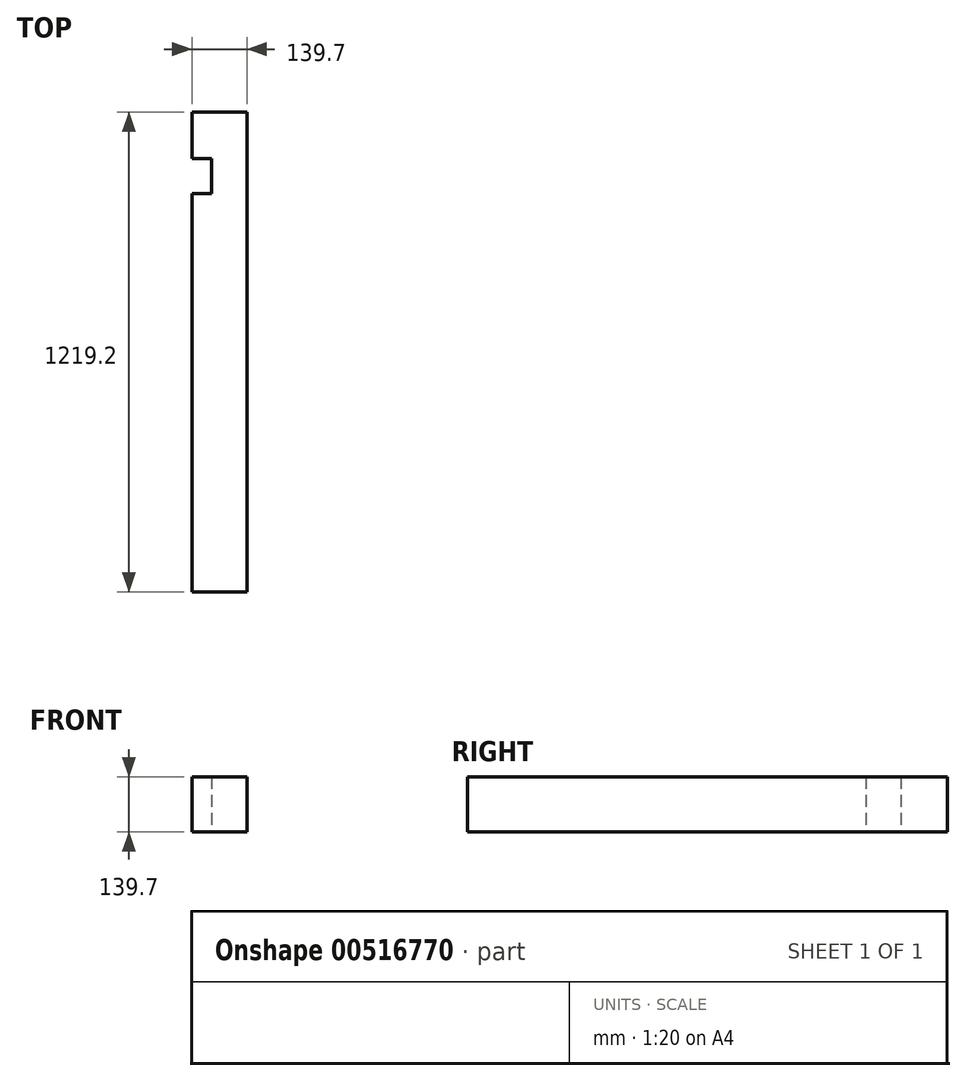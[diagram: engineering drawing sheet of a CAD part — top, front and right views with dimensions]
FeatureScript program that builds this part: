
annotation { "Feature Type Name" : "Feature", "Feature Type Description" : "" }
export const myFeature = defineFeature(function(context is Context, id is Id, definition is map)
    precondition{}
    {
        {
            var Q0;
            Q0=qCreatedBy(makeId("Front.planeOp"),FACE);
            var sketch = newSketch(context, id + "F0", { "sketchPlane" : qUnion([Q0])});
            skLineSegment(sketch, "E0.bottom", {"start": v(0, 0) * mm, "end": v(139.7, 0) * mm});
            skLineSegment(sketch, "E0.top", {"start": v(0, 139.7) * mm, "end": v(139.7, 139.7) * mm});
            skLineSegment(sketch, "E0.left", {"start": v(0, 0) * mm, "end": v(0, 139.7) * mm});
            skLineSegment(sketch, "E0.right", {"start": v(139.7, 0) * mm, "end": v(139.7, 139.7) * mm});
            skSolve(sketch);
        }
        {
            var Q0;
            Q0 = qSketchRegion(id + "F0", true);
            extrude(context, id + "F1", {"entities" : qUnion([Q0]), "depth" : 1219.2 * mm, "offsetDistance" : 25.4 * mm});
        }
        {
            var Q0;
            Q0=makeQuery(id+"F1.opExtrude","SWEPT_FACE",FACE,{"disambiguationData":[OSD([sQuery(id+"F0.wireOp",EDGE,"E0.left")])]});
            var sketch = newSketch(context, id + "F2", { "sketchPlane" : qUnion([Q0])});
            skLineSegment(sketch, "E1", {"start": v(118.76, 139.7) * mm, "end": v(118.76, 0) * mm});
            skLineSegment(sketch, "E2", {"start": v(207.66, 139.7) * mm, "end": v(207.66, 0) * mm});
            skLineSegment(sketch, "E3", {"start": v(207.66, 0) * mm, "end": v(118.76, 0) * mm});
            skLineSegment(sketch, "E4", {"start": v(118.76, 139.7) * mm, "end": v(207.66, 139.7) * mm});
            skLineSegment(sketch, "E5", {"start": v(118.76, 139.7) * mm, "end": v(0, 139.7) * mm});
            skLineSegment(sketch, "E6", {"start": v(0, 0) * mm, "end": v(118.76, 0) * mm});
            skSolve(sketch);
        }
        {
            var Q0;
            Q0=makeQuery(id+"F2.imprint","IMPRINT",FACE,{"disambiguationData":[TD([[makeQuery(id+"F2.imprint","IMPRINT",EDGE,{"derivedFrom":sQuery(id+"F2.wireOp",EDGE,"E1")}),1.0]])]});
            extrude(context, id + "F3", {"entities" : qUnion([Q0]), "operationType" : NewBodyOperationType.REMOVE, "oppositeDirection" : true, "depth" : 50.8 * mm, "offsetDistance" : 25.4 * mm});
        }
    });
